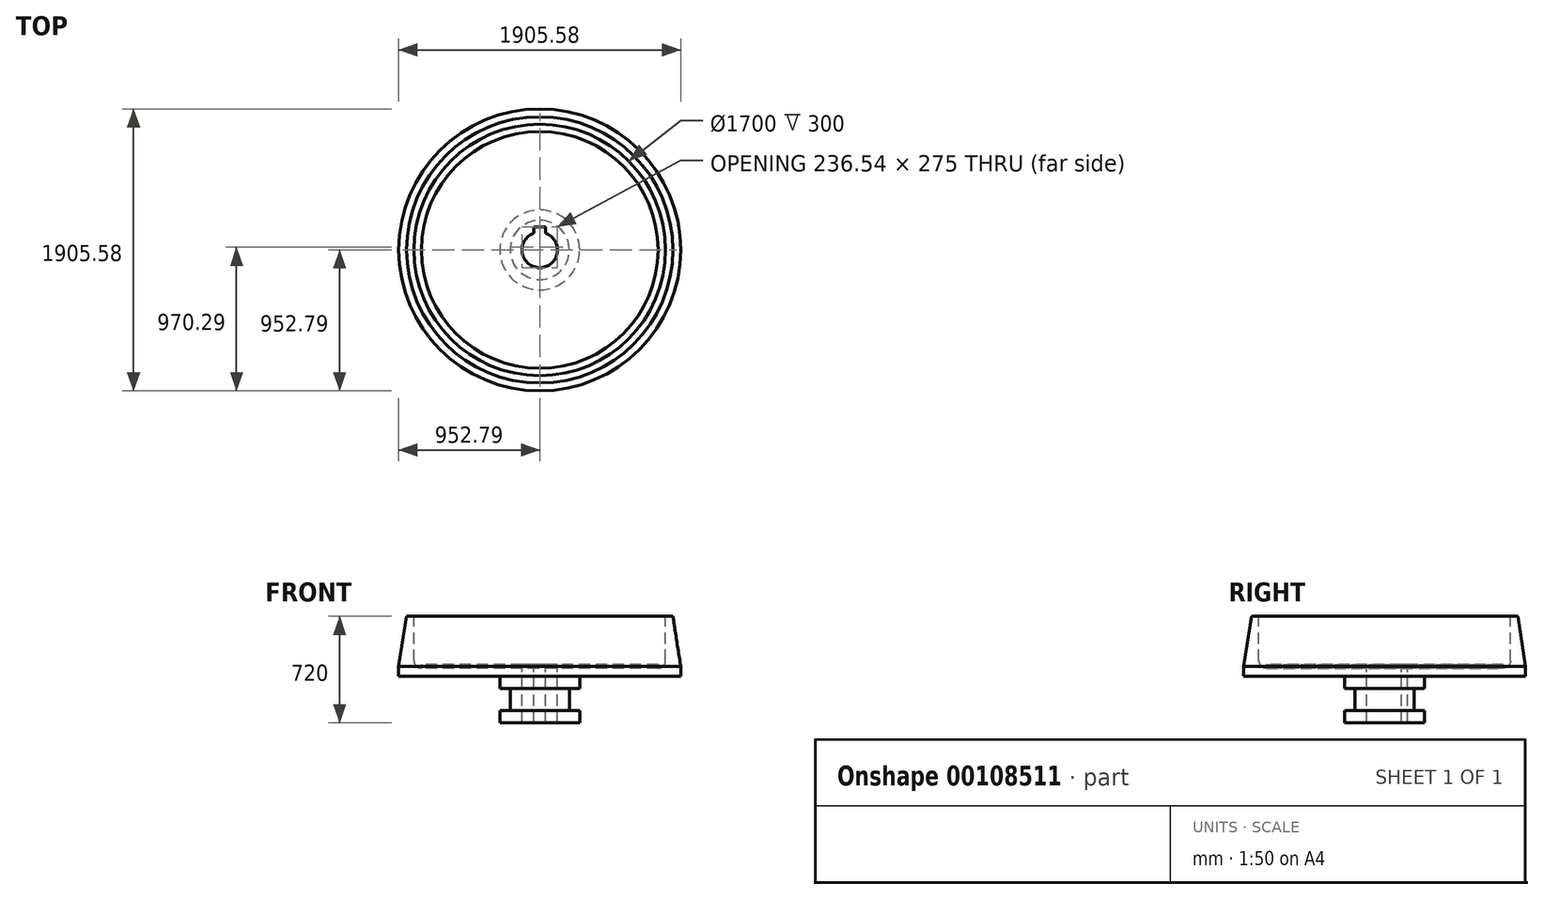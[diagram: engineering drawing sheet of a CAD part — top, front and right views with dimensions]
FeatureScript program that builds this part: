
annotation { "Feature Type Name" : "Feature", "Feature Type Description" : "" }
export const myFeature = defineFeature(function(context is Context, id is Id, definition is map)
    precondition{}
    {
        {
            var Q0;
            Q0=qCreatedBy(makeId("Front.planeOp"),FACE);
            var sketch = newSketch(context, id + "F0", { "sketchPlane" : qUnion([Q0])});
            skLineSegment(sketch, "E0", {"start": v(0, 344.4) * mm, "end": v(0, -378.62) * mm, "construction": true});
            skLineSegment(sketch, "E1", {"start": v(120, 0) * mm, "end": v(270, 0) * mm});
            skLineSegment(sketch, "E2", {"start": v(270, 0) * mm, "end": v(270, 83.72) * mm});
            skLineSegment(sketch, "E3", {"start": v(270, 83.72) * mm, "end": v(200, 83.72) * mm});
            skLineSegment(sketch, "E4", {"start": v(200, 83.72) * mm, "end": v(200, 233.72) * mm});
            skLineSegment(sketch, "E5", {"start": v(200, 233.72) * mm, "end": v(270, 233.72) * mm});
            skLineSegment(sketch, "E6", {"start": v(270, 233.72) * mm, "end": v(270, 313.72) * mm});
            skLineSegment(sketch, "E7", {"start": v(120, 0) * mm, "end": v(120, 370) * mm});
            skLineSegment(sketch, "E8", {"start": v(120, 370) * mm, "end": v(800, 370) * mm});
            skLineSegment(sketch, "E9", {"start": v(850, 420) * mm, "end": v(850, 720) * mm});
            skLineSegment(sketch, "E10", {"start": v(850, 720) * mm, "end": v(900, 720) * mm});
            skLineSegment(sketch, "E11", {"start": v(900, 720) * mm, "end": v(952.8, 382.13) * mm});
            skPoint(sketch, "E12.visualSharp", {"position": v(850, 370) * mm});
            skArc(sketch, "E12.filletArc", {"start": v(800, 370) * mm, "mid": v(835.36, 384.64) * mm, "end": v(850, 420) * mm});
            skLineSegment(sketch, "E13", {"start": v(952.8, 313.72) * mm, "end": v(952.8, 382.13) * mm});
            skLineSegment(sketch, "E14", {"start": v(270, 313.72) * mm, "end": v(952.8, 313.72) * mm});
            skSolve(sketch);
        }
        {
            var Q0;
            Q0 = qSketchRegion(id + "F0", true);
            var Q1;
            Q1=sQuery(id+"F0.wireOp",EDGE,"E0");
            revolve(context, id + "F1", {"entities" : qUnion([Q0]), "axis" : qUnion([Q1]), "revolveType" : RevolveType.FULL});
        }
        {
            var Q0;
            Q0=makeQuery(id+"F1.opRevolve","SWEPT_FACE",FACE,{"disambiguationData":[OSD([sQuery(id+"F0.wireOp",EDGE,"E8")])]});
            var sketch = newSketch(context, id + "F2", { "sketchPlane" : qUnion([Q0])});
            skSolve(sketch);
        }
        {
            var Q0;
            {var subQ0=sQuery(id+"F0.wireOp",EDGE,"E8");Q0=makeQuery(id+"F2.imprint","IMPRINT",FACE,{"disambiguationData":[TD([[makeQuery(id+"F2.imprint","IMPRINT",EDGE,{"derivedFrom":makeQuery(id+"F1.opRevolve","SWEPT_EDGE",EDGE,{"disambiguationData":[OSD([sQuery(id+"F0.wireOp",EDGE,"E7"),subQ0])]})}),-1.0]])]});}
            extrude(context, id + "F3", {"entities" : qUnion([Q0]), "operationType" : NewBodyOperationType.ADD, "depth" : 25 * mm});
        }
        {
            var Q0;
            Q0=makeQuery(id+"F3.opExtrude","CAP_FACE",FACE,{"disambiguationData":[OSD([sQuery(id+"F0.wireOp",EDGE,"E7"),sQuery(id+"F0.wireOp",EDGE,"E8"),sQuery(id+"F0.wireOp",EDGE,"E12.filletArc")])],"isStart":false});
            var sketch = newSketch(context, id + "F4", { "sketchPlane" : qUnion([Q0])});
            skLineSegment(sketch, "E15.bottom", {"start": v(40, 155) * mm, "end": v(-40, 155) * mm});
            skLineSegment(sketch, "E15.top", {"start": v(40, 85) * mm, "end": v(-40, 85) * mm});
            skLineSegment(sketch, "E15.left", {"start": v(40, 155) * mm, "end": v(40, 85) * mm});
            skLineSegment(sketch, "E15.right", {"start": v(-40, 155) * mm, "end": v(-40, 85) * mm});
            skPoint(sketch, "E15.middle", {"position": v(0, 120) * mm});
            skSolve(sketch);
        }
        {
            var Q0;
            Q0 = qSketchRegion(id + "F4", true);
            extrude(context, id + "F5", {"entities" : qUnion([Q0]), "operationType" : NewBodyOperationType.REMOVE, "endBound" : BoundingType.THROUGH_ALL, "oppositeDirection" : true, "depth" : 25 * mm});
        }
    });
